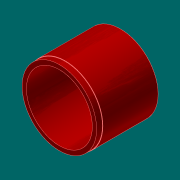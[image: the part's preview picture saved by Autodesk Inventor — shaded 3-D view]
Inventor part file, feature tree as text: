
AUTODESK INVENTOR PART (.ipt)
format: ipt  version: 2017.3 (Build 213257000, 257)  size: 111,104 bytes
history: native  units: in
note: dims shown in document units (in); Inventor stores cm internally (conversion verified against a paired STEP export)
features: extrude x2, sketch x2, fillet x1, chamfer x1
ambient origin geometry x8: Origin, YZ Plane, XZ Plane, XY Plane, X Axis, Y Axis, Z Axis, Center Point
bodies: Solid1 (feature_tree)
feature tree (6):
  extrude  "Extrusion1"  Depth=12.73in
  extrude  "Extrusion2"  Depth=0.0312in
  fillet  "Fillet1"  Radius=1.0in
  chamfer  "Chamfer1"  Distance=0.0312in
  sketch  "Sketch1"  dims[d0=11.1417in d1=12.73in]
  sketch  "Sketch2"  dims[d2=10.3543in d3=0.0in d4=12.605in d5=1.0in d6=0.0in d10=0.0312in d11=0.0312in d12=0.125in d13=45.0deg]
